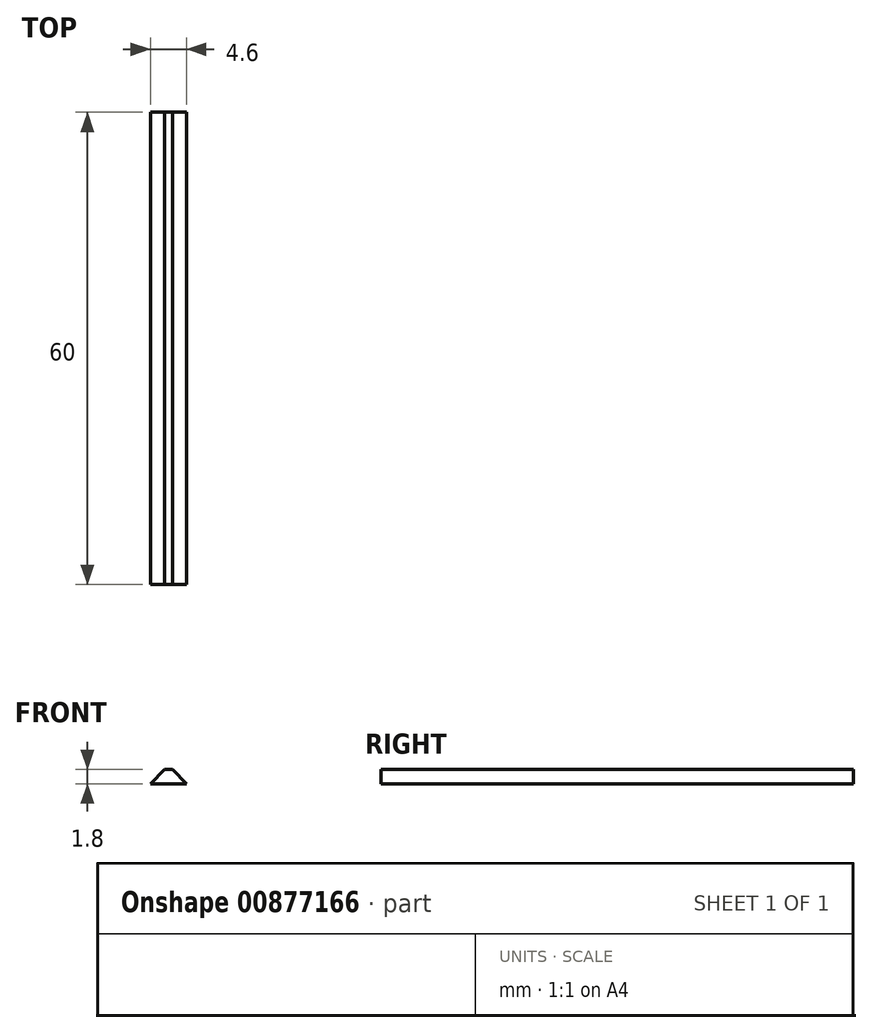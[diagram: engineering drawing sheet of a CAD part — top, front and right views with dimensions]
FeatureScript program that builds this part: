
annotation { "Feature Type Name" : "Feature", "Feature Type Description" : "" }
export const myFeature = defineFeature(function(context is Context, id is Id, definition is map)
    precondition{}
    {
        {
            var Q0;
            Q0=qCreatedBy(makeId("Front.planeOp"),FACE);
            var sketch = newSketch(context, id + "F0", { "sketchPlane" : qUnion([Q0])});
            skLineSegment(sketch, "E0.bottom", {"start": v(-2.3, 0) * mm, "end": v(2.3, 0) * mm});
            skLineSegment(sketch, "E0.top", {"start": v(-2.3, -1.8) * mm, "end": v(2.3, -1.8) * mm});
            skLineSegment(sketch, "E0.left", {"start": v(-2.3, 0) * mm, "end": v(-2.3, -1.8) * mm});
            skLineSegment(sketch, "E0.right", {"start": v(2.3, 0) * mm, "end": v(2.3, -1.8) * mm});
            skLineSegment(sketch, "E1", {"start": v(-2.3, -1.8) * mm, "end": v(-0.5, 0) * mm});
            skLineSegment(sketch, "E2", {"start": v(2.3, -1.8) * mm, "end": v(0.5, 0) * mm});
            skSolve(sketch);
        }
        {
            var Q0;
            Q0=makeQuery(id+"F0.imprint","IMPRINT",FACE,{"disambiguationData":[TD([[makeQuery(id+"F0.imprint","IMPRINT",EDGE,{"derivedFrom":sQuery(id+"F0.wireOp",EDGE,"E0.top")}),1.0]])]});
            extrude(context, id + "F1", {"entities" : qUnion([Q0]), "depth" : 60 * mm, "offsetDistance" : 25 * mm});
        }
    });
